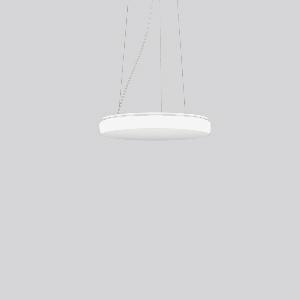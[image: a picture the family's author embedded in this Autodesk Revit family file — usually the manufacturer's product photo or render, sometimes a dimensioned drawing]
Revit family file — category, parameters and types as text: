
# Revit family: flat_polymero_kreis_slim_312241_002_2_76_c782
name_source: partatom
category: Lighting Fixtures
units: mm (PartAtom-declared; Revit-internal decimal feet)

## family parameters
Cut with Voids When Loaded = No
Host = Face
Light Source = No
Part Type = Normal
Room Calculation Point = No
Round Connector Dimension = Use Diameter
Shared = No

## types (1)
- FLAT POLYMERO KREIS SLIM (1 x LED Modul 830, 3300 lm, 3000)
    Apparent Load = 32 VA
    CIE Flux Codes = 42 73 92 87 100
    Color Rendering = 80
    Color Temperature = 3000
    Default Elevation = 1800 mm
    Description = Series: FLAT POLYMERO KREIS SLIM
Decorative round LED pendant luminaire. Base and canopy: metal, powder-coated, white. Canopy Ø 205 mm, h 35 mm. Diffuser made of plastic (polycarbonate), opal, shockproof. Diffuser fastening: patented push system. Homogeneous and smooth light distribution. Suitable for pendant. 3-point steel cable suspension, steplessly adjustable. Special lengths available on request. TouchDim sensor capable. Light and/or presence sensors can be integrated. 
Colour: white
Diameter: 460 mm
Height: 68 mm
Suspension length: 200-1300 mm
Lamp: LED exchangeable
Socket: without socket
Colour temperature: 3000K
Colour rendering index (CRI): 83
System power: 32 W
Rated luminous flux: 3300 lm
Luminous efficiency: 103 lm/W
Control gear: AC power, DALI dimmable
Protection class: I
Type of protection: IP 40
    Height = 68 mm
    Lamp = 1 x LED Modul 830
    Lamp Light Flux = 3300 lm
    Lamp count = 1
    Length = 460 mm
    Lifetime = 50000 h
    Luminous efficacy = 103 lm/W
    Manufacturer = RZB
    ModVariant = No
    Model = 312241.002.2.76
    Mounting Place = Ceiling
    Mounting Type = Pendant
    Number of Poles = 1
    OnlyDefault = Yes
    Power Factor = 1
    Product Name = FLAT POLYMERO KREIS SLIM
    Product group = Pendant luminaires
    ProductGroupID = 902
    Protection Class = Protection class I
    Protection Degree = IP 40
    RLX_Detail_Level = 1
    RLX_Emergency_Light_Flux = 0 lm
    RLX_Emergency_Type = 0
    RLX_Emergency_Type_DB = No
    RlxData = <blob elided: 58093 chars, md5=00177d2c>
    Socket = socket
    Standby Power = 0 W
    System Light Flux = 3300 lm
    System Power = 32 W
    Type Comments = Product without accessories
    Type Image = 312090.002.jpg
    URL = http://relux.com
    VarID = ---
    Voltage = 230 V
    Voltage Range = 220-240 V
    Weight = 0.00 kg
    Width = 0 mm  [stored 0 ft]

note: [stored X ft] marks values corroborated as IEEE doubles in the binary element streams (Revit-internal decimal feet)

## geometry (parser evidence)
native form markers: Blend x4, Sweep x12
no freeform markers — native parametric forms only
